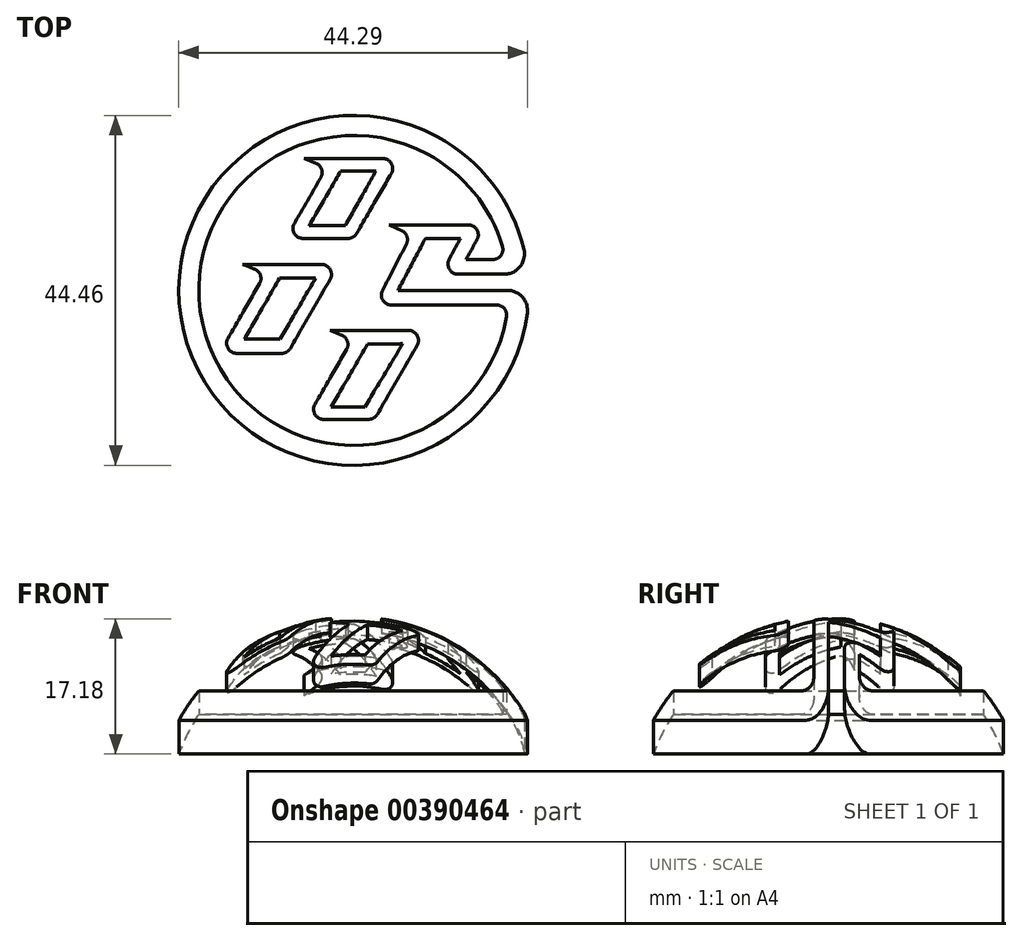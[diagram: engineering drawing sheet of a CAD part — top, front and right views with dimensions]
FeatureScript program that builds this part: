
annotation { "Feature Type Name" : "Feature", "Feature Type Description" : "" }
export const myFeature = defineFeature(function(context is Context, id is Id, definition is map)
    precondition{}
    {
        {
            var Q0;
            Q0=qCreatedBy(makeId("Top.planeOp"),FACE);
            var sketch = newSketch(context, id + "F0", { "sketchPlane" : qUnion([Q0])});
            skArc(sketch, "E0", {"start": v(21.6, 5.2) * mm, "mid": v(-22.2, -1.18) * mm, "end": v(22.04, -2.87) * mm});
            skArc(sketch, "E1", {"start": v(18.88, 5.56) * mm, "mid": v(-19.65, -1.14) * mm, "end": v(19.4, -3.35) * mm});
            skLineSegment(sketch, "E2", {"start": v(-6.33, 16.76) * mm, "end": v(3.67, 16.76) * mm});
            skLineSegment(sketch, "E3", {"start": v(4.77, 14.86) * mm, "end": v(0.37, 7.24) * mm});
            skLineSegment(sketch, "E4", {"start": v(-0.73, 6.6) * mm, "end": v(-6.45, 6.6) * mm});
            skLineSegment(sketch, "E5", {"start": v(-7.55, 8.5) * mm, "end": v(-4.19, 14.34) * mm});
            skLineSegment(sketch, "E6", {"start": v(-4.81, 16.15) * mm, "end": v(-6.33, 16.76) * mm});
            skLineSegment(sketch, "E7", {"start": v(-14.1, 3.3) * mm, "end": v(-4.1, 3.3) * mm});
            skLineSegment(sketch, "E8", {"start": v(-3, 1.4) * mm, "end": v(-8.07, -7.37) * mm});
            skLineSegment(sketch, "E9", {"start": v(-9.17, -8) * mm, "end": v(-14.88, -8) * mm});
            skLineSegment(sketch, "E10", {"start": v(-15.98, -6.1) * mm, "end": v(-11.96, 0.88) * mm});
            skLineSegment(sketch, "E11", {"start": v(-12.58, 2.69) * mm, "end": v(-14.1, 3.3) * mm});
            skLineSegment(sketch, "E12", {"start": v(-3.05, -5.08) * mm, "end": v(6.94, -5.08) * mm});
            skLineSegment(sketch, "E13", {"start": v(8.04, -6.98) * mm, "end": v(2.98, -15.75) * mm});
            skLineSegment(sketch, "E14", {"start": v(1.88, -16.38) * mm, "end": v(-3.83, -16.38) * mm});
            skLineSegment(sketch, "E15", {"start": v(-4.93, -14.48) * mm, "end": v(-0.9, -7.5) * mm});
            skLineSegment(sketch, "E16", {"start": v(-1.53, -5.7) * mm, "end": v(-3.05, -5.08) * mm});
            skPoint(sketch, "E17.visualSharp", {"position": v(5.87, 16.76) * mm});
            skArc(sketch, "E17.filletArc", {"start": v(4.77, 14.86) * mm, "mid": v(4.77, 16.13) * mm, "end": v(3.67, 16.76) * mm});
            skPoint(sketch, "E18.visualSharp", {"position": v(-3.46, 15.6) * mm});
            skArc(sketch, "E18.filletArc", {"start": v(-4.19, 14.34) * mm, "mid": v(-4.09, 15.39) * mm, "end": v(-4.81, 16.15) * mm});
            skPoint(sketch, "E19.visualSharp", {"position": v(-8.65, 6.6) * mm});
            skArc(sketch, "E19.filletArc", {"start": v(-7.55, 8.5) * mm, "mid": v(-7.55, 7.24) * mm, "end": v(-6.45, 6.6) * mm});
            skPoint(sketch, "E20.visualSharp", {"position": v(0, 6.6) * mm});
            skArc(sketch, "E20.filletArc", {"start": v(-0.73, 6.6) * mm, "mid": v(-0.1, 6.77) * mm, "end": v(0.37, 7.24) * mm});
            skPoint(sketch, "E21.visualSharp", {"position": v(-17.08, -8) * mm});
            skArc(sketch, "E21.filletArc", {"start": v(-15.98, -6.1) * mm, "mid": v(-15.98, -7.37) * mm, "end": v(-14.88, -8) * mm});
            skPoint(sketch, "E22.visualSharp", {"position": v(-11.23, 2.14) * mm});
            skArc(sketch, "E22.filletArc", {"start": v(-11.96, 0.88) * mm, "mid": v(-11.86, 1.93) * mm, "end": v(-12.58, 2.69) * mm});
            skPoint(sketch, "E23.visualSharp", {"position": v(-1.9, 3.3) * mm});
            skArc(sketch, "E23.filletArc", {"start": v(-3, 1.4) * mm, "mid": v(-3, 2.67) * mm, "end": v(-4.1, 3.3) * mm});
            skPoint(sketch, "E24.visualSharp", {"position": v(-8.43, -8) * mm});
            skArc(sketch, "E24.filletArc", {"start": v(-9.17, -8) * mm, "mid": v(-8.53, -7.83) * mm, "end": v(-8.07, -7.37) * mm});
            skPoint(sketch, "E25.visualSharp", {"position": v(-6.03, -16.38) * mm});
            skArc(sketch, "E25.filletArc", {"start": v(-4.93, -14.48) * mm, "mid": v(-4.93, -15.75) * mm, "end": v(-3.83, -16.38) * mm});
            skPoint(sketch, "E26.visualSharp", {"position": v(-0.18, -6.24) * mm});
            skArc(sketch, "E26.filletArc", {"start": v(-0.9, -7.5) * mm, "mid": v(-0.8, -6.46) * mm, "end": v(-1.53, -5.7) * mm});
            skPoint(sketch, "E27.visualSharp", {"position": v(9.14, -5.08) * mm});
            skArc(sketch, "E27.filletArc", {"start": v(8.04, -6.98) * mm, "mid": v(8.04, -5.71) * mm, "end": v(6.94, -5.08) * mm});
            skPoint(sketch, "E28.visualSharp", {"position": v(2.62, -16.38) * mm});
            skArc(sketch, "E28.filletArc", {"start": v(1.88, -16.38) * mm, "mid": v(2.52, -16.21) * mm, "end": v(2.98, -15.75) * mm});
            skLineSegment(sketch, "E29", {"start": v(17.66, 3.93) * mm, "end": v(14.24, 3.93) * mm});
            skLineSegment(sketch, "E30", {"start": v(14.24, 3.93) * mm, "end": v(15.65, 6.43) * mm});
            skLineSegment(sketch, "E31", {"start": v(14.55, 8.33) * mm, "end": v(4.49, 8.33) * mm});
            skLineSegment(sketch, "E32", {"start": v(4.49, 8.33) * mm, "end": v(6.07, 7.6) * mm});
            skLineSegment(sketch, "E33", {"start": v(6.67, 5.86) * mm, "end": v(3.65, 0) * mm});
            skLineSegment(sketch, "E34", {"start": v(4.78, -1.86) * mm, "end": v(18.15, -1.86) * mm});
            skPoint(sketch, "E35.visualSharp", {"position": v(7.28, 7.04) * mm});
            skArc(sketch, "E35.filletArc", {"start": v(6.67, 5.86) * mm, "mid": v(6.74, 6.86) * mm, "end": v(6.07, 7.6) * mm});
            skPoint(sketch, "E36.visualSharp", {"position": v(2.7, -1.86) * mm});
            skArc(sketch, "E36.filletArc", {"start": v(3.65, 0) * mm, "mid": v(3.7, -1.25) * mm, "end": v(4.78, -1.86) * mm});
            skPoint(sketch, "E37.visualSharp", {"position": v(16.72, 8.33) * mm});
            skArc(sketch, "E37.filletArc", {"start": v(15.65, 6.43) * mm, "mid": v(15.64, 7.7) * mm, "end": v(14.55, 8.33) * mm});
            skLineSegment(sketch, "E38", {"start": v(19.14, 2.06) * mm, "end": v(13.24, 2.06) * mm});
            skLineSegment(sketch, "E39", {"start": v(12.12, 3.94) * mm, "end": v(13.56, 6.6) * mm});
            skLineSegment(sketch, "E40", {"start": v(13.56, 6.6) * mm, "end": v(9.1, 6.6) * mm});
            skLineSegment(sketch, "E41", {"start": v(9.1, 6.6) * mm, "end": v(5.6, 0) * mm});
            skLineSegment(sketch, "E42", {"start": v(5.6, 0) * mm, "end": v(19.52, 0) * mm});
            skPoint(sketch, "E43.visualSharp", {"position": v(19.29, 3.93) * mm});
            skArc(sketch, "E43.filletArc", {"start": v(17.66, 3.93) * mm, "mid": v(18.68, 4.44) * mm, "end": v(18.88, 5.56) * mm});
            skPoint(sketch, "E44.visualSharp", {"position": v(19.6, -1.86) * mm});
            skArc(sketch, "E44.filletArc", {"start": v(19.4, -3.35) * mm, "mid": v(19.12, -2.31) * mm, "end": v(18.15, -1.86) * mm});
            skPoint(sketch, "E45.visualSharp", {"position": v(22.13, 2.06) * mm});
            skArc(sketch, "E45.filletArc", {"start": v(19.14, 2.06) * mm, "mid": v(21.13, 3.03) * mm, "end": v(21.6, 5.2) * mm});
            skPoint(sketch, "E46.visualSharp", {"position": v(22.23, 0) * mm});
            skArc(sketch, "E46.filletArc", {"start": v(22.04, -2.87) * mm, "mid": v(21.43, -0.86) * mm, "end": v(19.52, 0) * mm});
            skLineSegment(sketch, "E47", {"start": v(-1.08, 8.22) * mm, "end": v(2.81, 15.15) * mm});
            skLineSegment(sketch, "E48", {"start": v(2.81, 15.15) * mm, "end": v(-1.67, 15.15) * mm});
            skLineSegment(sketch, "E49", {"start": v(-1.67, 15.15) * mm, "end": v(-5.68, 8.2) * mm});
            skLineSegment(sketch, "E50", {"start": v(-5.68, 8.2) * mm, "end": v(-1.08, 8.22) * mm});
            skLineSegment(sketch, "E51", {"start": v(-4.84, 1.6) * mm, "end": v(-9.4, 1.6) * mm});
            skLineSegment(sketch, "E52", {"start": v(-9.4, 1.6) * mm, "end": v(-13.91, -6.2) * mm});
            skLineSegment(sketch, "E53", {"start": v(-13.91, -6.2) * mm, "end": v(-9.35, -6.2) * mm});
            skLineSegment(sketch, "E54", {"start": v(-9.35, -6.2) * mm, "end": v(-4.84, 1.6) * mm});
            skLineSegment(sketch, "E55", {"start": v(1.76, -6.8) * mm, "end": v(-2.86, -14.8) * mm});
            skLineSegment(sketch, "E56", {"start": v(-2.86, -14.8) * mm, "end": v(1.4, -14.8) * mm});
            skLineSegment(sketch, "E57", {"start": v(1.4, -14.8) * mm, "end": v(6.21, -6.78) * mm});
            skLineSegment(sketch, "E58", {"start": v(6.21, -6.78) * mm, "end": v(1.76, -6.8) * mm});
            skPoint(sketch, "E59.visualSharp", {"position": v(11.1, 2.06) * mm});
            skArc(sketch, "E59.filletArc", {"start": v(12.12, 3.94) * mm, "mid": v(12.14, 2.68) * mm, "end": v(13.24, 2.06) * mm});
            skSolve(sketch);
        }
        {
            var Q0;
            Q0=makeQuery(id+"F0.imprint","IMPRINT",FACE,{"disambiguationData":[TD([[makeQuery(id+"F0.imprint","IMPRINT",EDGE,{"derivedFrom":sQuery(id+"F0.wireOp",EDGE,"E2")}),-1.0]])]});
            var Q1;
            Q1=makeQuery(id+"F0.imprint","IMPRINT",FACE,{"disambiguationData":[TD([[makeQuery(id+"F0.imprint","IMPRINT",EDGE,{"derivedFrom":sQuery(id+"F0.wireOp",EDGE,"E0")}),1.0]])]});
            var Q2;
            Q2=makeQuery(id+"F0.imprint","IMPRINT",FACE,{"disambiguationData":[TD([[makeQuery(id+"F0.imprint","IMPRINT",EDGE,{"derivedFrom":sQuery(id+"F0.wireOp",EDGE,"E12")}),-1.0]])]});
            var Q3;
            Q3=makeQuery(id+"F0.imprint","IMPRINT",FACE,{"disambiguationData":[TD([[makeQuery(id+"F0.imprint","IMPRINT",EDGE,{"derivedFrom":sQuery(id+"F0.wireOp",EDGE,"E7")}),-1.0]])]});
            extrude(context, id + "F1", {"entities" : qUnion([Q0, Q1, Q2, Q3]), "depth" : 25.4 * mm});
        }
        {
            var Q0;
            Q0=qCreatedBy(makeId("Right.planeOp"),FACE);
            var sketch = newSketch(context, id + "F2", { "sketchPlane" : qUnion([Q0])});
            skLineSegment(sketch, "E60.0", {"start": v(0, 0) * mm, "end": v(22.23, 0) * mm});
            skArc(sketch, "E61", {"start": v(25.4, 0) * mm, "mid": v(17.96, 17.96) * mm, "end": v(0, 25.4) * mm});
            skArc(sketch, "E62", {"start": v(23.62, 0) * mm, "mid": v(16.7, 16.7) * mm, "end": v(0, 23.62) * mm});
            skLineSegment(sketch, "E63", {"start": v(22.23, 0) * mm, "end": v(23.62, 0) * mm});
            skLineSegment(sketch, "E64", {"start": v(23.62, 0) * mm, "end": v(25.4, 0) * mm, "construction": true});
            skLineSegment(sketch, "E65", {"start": v(0, 25.4) * mm, "end": v(25.4, 25.4) * mm, "construction": true});
            skLineSegment(sketch, "E66", {"start": v(25.4, 25.4) * mm, "end": v(25.4, 0) * mm, "construction": true});
            skPoint(sketch, "E67.orphan", {"position": v(-22.23, 0) * mm});
            skLineSegment(sketch, "E68", {"start": v(0, 0) * mm, "end": v(0, 23.62) * mm});
            skLineSegment(sketch, "E69", {"start": v(0, 23.62) * mm, "end": v(0, 25.4) * mm, "construction": true});
            skLineSegment(sketch, "E70", {"start": v(0, 25.4) * mm, "end": v(0, 26.67) * mm});
            skLineSegment(sketch, "E71", {"start": v(0, 26.67) * mm, "end": v(26.67, 26.67) * mm});
            skLineSegment(sketch, "E72", {"start": v(26.67, 26.67) * mm, "end": v(26.67, 0) * mm});
            skLineSegment(sketch, "E73", {"start": v(26.67, 0) * mm, "end": v(25.4, 0) * mm});
            skSolve(sketch);
        }
        {
            var Q0;
            Q0=makeQuery(id+"F2.imprint","IMPRINT",FACE,{"disambiguationData":[TD([[makeQuery(id+"F2.imprint","IMPRINT",EDGE,{"derivedFrom":sQuery(id+"F2.wireOp",EDGE,"E60.0")}),1.0]])]});
            var Q1;
            Q1=sQuery(id+"F2.wireOp",EDGE,"E68");
            revolve(context, id + "F3", {"operationType" : NewBodyOperationType.REMOVE, "entities" : qUnion([Q0]), "axis" : qUnion([Q1]), "revolveType" : RevolveType.FULL, "oppositeDirection" : true});
        }
        {
            var Q0;
            Q0=makeQuery(id+"F2.imprint","IMPRINT",FACE,{"disambiguationData":[TD([[makeQuery(id+"F2.imprint","IMPRINT",EDGE,{"derivedFrom":sQuery(id+"F2.wireOp",EDGE,"E61")}),-1.0]])]});
            var Q1;
            Q1=sQuery(id+"F2.wireOp",EDGE,"E68");
            revolve(context, id + "F4", {"operationType" : NewBodyOperationType.REMOVE, "entities" : qUnion([Q0]), "axis" : qUnion([Q1]), "revolveType" : RevolveType.FULL, "oppositeDirection" : true});
        }
    });
